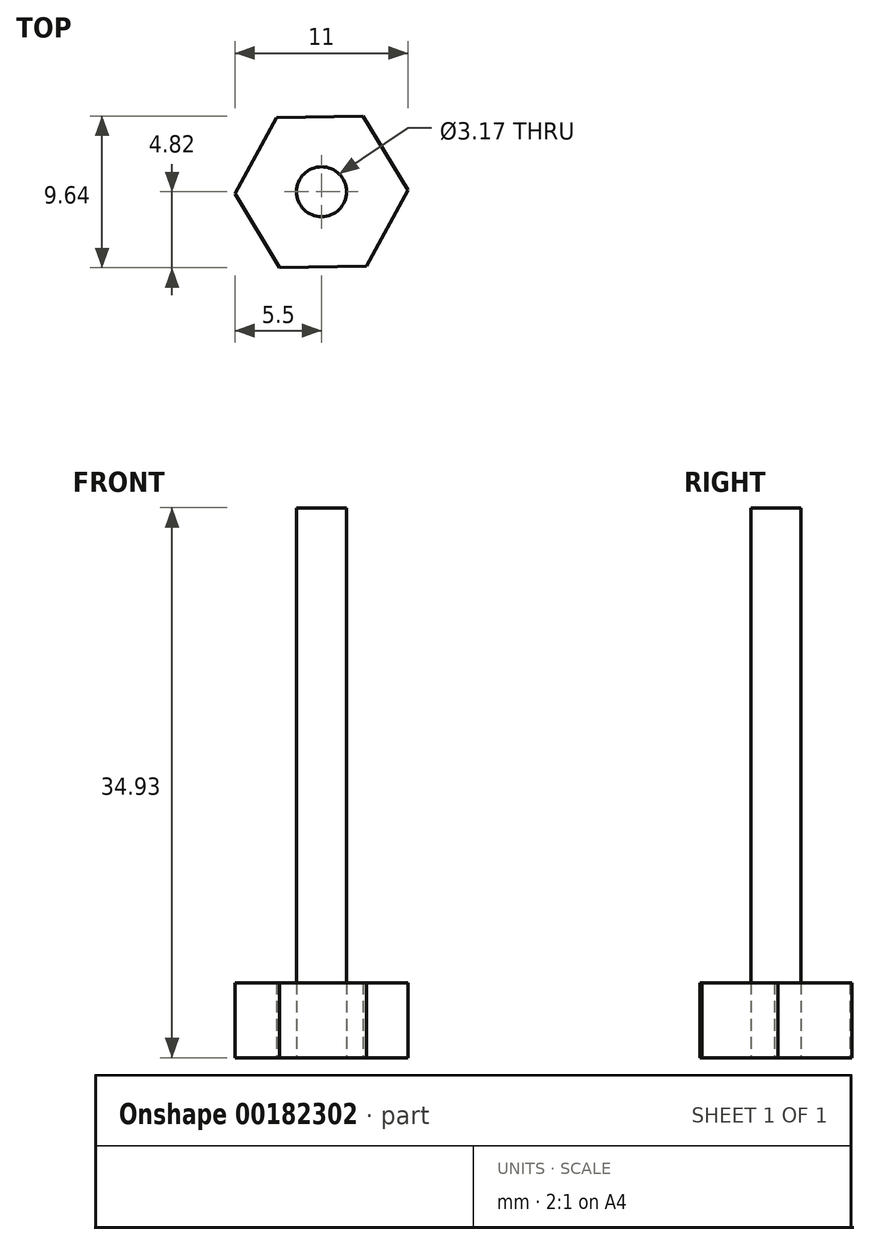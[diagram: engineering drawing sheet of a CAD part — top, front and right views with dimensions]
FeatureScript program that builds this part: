
annotation { "Feature Type Name" : "Feature", "Feature Type Description" : "" }
export const myFeature = defineFeature(function(context is Context, id is Id, definition is map)
    precondition{}
    {
        {
            var Q0;
            Q0=qCreatedBy(makeId("Top.planeOp"),FACE);
            var sketch = newSketch(context, id + "F0", { "sketchPlane" : qUnion([Q0])});
            skCircle(sketch, "E0.cCircle", {"center": v(0, 0) * mm, "radius": 4.76 * mm, "construction": true});
            skLineSegment(sketch, "E0.0", {"start": v(5.5, 0.11) * mm, "end": v(2.85, -4.7) * mm});
            skLineSegment(sketch, "E0.1", {"start": v(2.85, -4.7) * mm, "end": v(-2.65, -4.82) * mm});
            skLineSegment(sketch, "E0.2", {"start": v(-2.65, -4.82) * mm, "end": v(-5.5, -0.11) * mm});
            skLineSegment(sketch, "E0.3", {"start": v(-5.5, -0.11) * mm, "end": v(-2.85, 4.7) * mm});
            skLineSegment(sketch, "E0.4", {"start": v(-2.85, 4.7) * mm, "end": v(2.65, 4.82) * mm});
            skLineSegment(sketch, "E0.5", {"start": v(2.65, 4.82) * mm, "end": v(5.5, 0.11) * mm});
            skPoint(sketch, "E0.0.midPoint", {"position": v(4.17, -2.3) * mm});
            skCircle(sketch, "E1", {"center": v(0, 0) * mm, "radius": 1.59 * mm});
            skSolve(sketch);
        }
        {
            var Q0;
            Q0 = qSketchRegion(id + "F0", true);
            extrude(context, id + "F1", {"entities" : qUnion([Q0]), "depth" : 4.76 * mm});
        }
        {
            var Q0;
            Q0=qCreatedBy(makeId("Top.planeOp"),FACE);
            var sketch = newSketch(context, id + "F2", { "sketchPlane" : qUnion([Q0])});
            skPoint(sketch, "E2.0.midPoint", {"position": v(0.78, -1.38) * mm});
            skCircle(sketch, "E3", {"center": v(0, 0) * mm, "radius": 1.59 * mm});
            skCircle(sketch, "E4.cCircle", {"center": v(0, 0) * mm, "radius": 1.3 * mm, "construction": true});
            skPoint(sketch, "E4.0.midPoint", {"position": v(-1.29, -0.2) * mm});
            skSolve(sketch);
        }
        {
            var Q0;
            Q0 = qSketchRegion(id + "F2", true);
            extrude(context, id + "F3", {"entities" : qUnion([Q0]), "depth" : 34.92 * mm});
        }
    });
